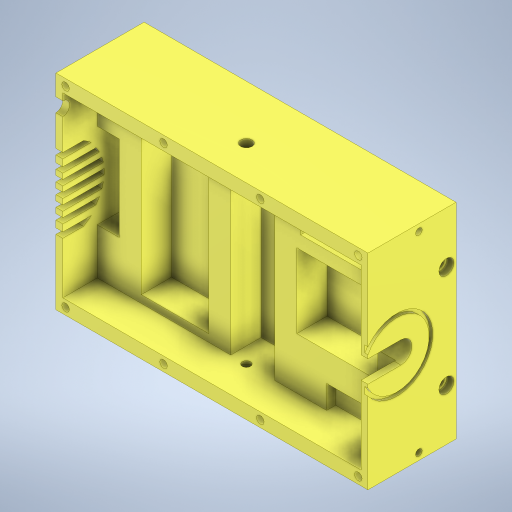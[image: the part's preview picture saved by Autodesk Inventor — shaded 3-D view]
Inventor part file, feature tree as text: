
AUTODESK INVENTOR PART (.ipt)
format: ipt  version: 2023 (Build 270158030, 158C)  size: 770,048 bytes
history: native  units: mm
features: sketch x20, extrude x16, projected_geometry x8, hole x7, mirror x1, plane x1
ambient origin geometry x8: Origin, YZ Plane, XZ Plane, XY Plane, X Axis, Y Axis, Z Axis, Center Point
bodies: Solid1 (feature_tree)
feature tree (53):
  extrude  "MainInnerBodyExtrusion"  Depth=149.0mm
  extrude  "HoleForCamerabase"  Depth=50.0mm
  extrude  "HoleForFan"  Depth=59.0mm
  extrude  "HoleForPi"  TaperAngle=0.0deg  [1 undecoded]
  extrude  "HoleForPoeAdapter"  Depth=62.0mm
  extrude  "HoleForThermister"  Depth=47.0mm
  extrude  "HoleForSensor"  Depth=32.0mm
  extrude  "SlotsForRearFan"  Depth=47.0mm
  extrude  "VentForCamera"  Depth=16.0mm
  extrude  "HoleForLens"  Depth=118.0mm
  sketch  "Sketch23"  dims[d26=49.0mm d27=118.0mm]
  hole  "Hole for 6-32 Insert"  [1 undecoded]
  hole  "Screw hole for 6-32 screw"  [1 undecoded]
  hole  "Side hole for 1-4 20 insert"  [1 undecoded]
  mirror  "Mirror for side insert"
  extrude  "Extrusion18"  Depth=17.0mm
  extrude  "HoleForPowerWire"  TaperAngle=0.0deg  [1 undecoded]
  extrude  "Extrusion22"  Depth=2.0mm
  extrude  "Extrusion23"  Depth=4.0mm
  extrude  "ExtrusionForBottom"  Depth=4.0mm
  extrude  "CutOutForFilter"  Depth=15.5mm
  hole  "Hole13"  [1 undecoded]
  hole  "Hole16"  [1 undecoded]
  hole  "Hole17"  [1 undecoded]
  plane  "Work Plane9"
  hole  "Hole19"  [1 undecoded]
  sketch  "Sketch1"  dims[d0=222.7mm d1=149.0mm]
  sketch  "Sketch3"  dims[d2=50.0mm d3=0.0mm d5=15.7mm]
  sketch  "Sketch4"  dims[d6=54.0mm d7=59.0mm]
  sketch  "Sketch6"  dims[d8=47.0mm d9=0.0mm]
  sketch  "Sketch7"  dims[d13=16.0mm d14=62.0mm]
  sketch  "Sketch11"  dims[d15=3.0mm d16=47.0mm]
  sketch  "Sketch15"  dims[d17=0.0mm d20=32.0mm]
  sketch  "Sketch16"  dims[d21=129.0mm d22=47.0mm]
  sketch  "Sketch18"  dims[d23=0.0mm d25=16.0mm]
  sketch  "Sketch24"  dims[d28=47.0mm d29=0.0mm]
  sketch  "Sketch25"  dims[d36=69.0mm d37=28.0mm]
  projected_geometry  "Projected Loop1"
  sketch  "Sketch26"  dims[d38=47.0mm d39=0.0mm]
  sketch  "Sketch37"  dims[d42=50.0mm d43=17.0mm]
  projected_geometry  "Projected Loop3"
  projected_geometry  "Projected Loop4"
  sketch  "Sketch39"  dims[d46=31.5mm d47=0.0mm]
  projected_geometry  "Projected Loop5"
  sketch  "Sketch43"  dims[d67=60.0mm d69=2.0mm]
  projected_geometry  "Projected Loop8"
  sketch  "Sketch47"  dims[d71=4.0mm d72=4.0mm]
  projected_geometry  "Projected Loop12"
  sketch  "Sketch55"  dims[d73=4.0mm d75=4.0mm]
  projected_geometry  "Projected Loop14"
  sketch  "Sketch56"  dims[d76=10.0mm d77=0.0mm d78=15.5mm]
  projected_geometry  "Projected Loop15"
  sketch  "Sketch60"  dims[d79=22.0mm d85=3.0mm d86=3.0mm d87=10.0mm d88=16.0mm d89=1.5mm d90=3.0mm d91=3.0mm d92=3.0mm d93=0.0mm d94=0.0mm d95=15.0mm d97=16.0mm d98=10.0mm d99=0.0mm d106=5.0mm d108=5.0mm d109=4.7mm d110=6.0mm d111=5.54mm d112=5.55mm d113=90.0deg d114=7.2mm d115=20.594885mm d116=3.797mm d117=6.0mm d118=12.7mm d119=2.362mm d120=90.0deg d121=15.0mm d122=20.594885mm d130=7.666mm d131=6.0mm d132=8.406mm d133=7.41mm d134=90.0deg d135=9.53mm d136=20.594885mm d137=24.0mm d138=10.0mm d139=3.0mm d140=25.0mm d141=0.0mm d142=30.0mm d144=10.0mm d145=0.0mm d222=76.2mm d223=76.2mm d224=76.2mm d225=76.2mm d226=25.0mm d227=111.350057mm d228=2.0mm d229=0.0mm d230=2.0mm d231=0.0mm d232=14.0mm d233=0.0mm d255=21.0mm d256=52.25mm d257=47.0mm d258=2.25mm d259=0.0mm d293=27.0mm d294=5.0mm d295=5.0mm d296=4.699mm d297=6.0mm d298=4.8514mm d299=5.55244mm d300=90.0deg d301=7.1374mm d302=0.0mm d336=7.0mm d337=37.25mm d338=37.25mm d339=7.142mm d340=6.0mm d341=11.0mm d342=5.0mm d343=90.0deg d344=152.4mm d345=0.0mm d346=7.0mm d347=7.142mm d348=6.0mm d349=11.0mm d350=5.0mm d351=90.0deg d352=127.0mm d353=0.0mm d354=-11.35mm d366=8.0mm d367=6.0mm d368=9.52mm d369=11.4mm d370=90.0deg d371=12.7mm d372=0.0mm]
note: 9 required parameter values undecoded (feature->parameter linkage not recoverable at this tier; creation-order binding heuristic only, values carry confidence <= 0.55)
